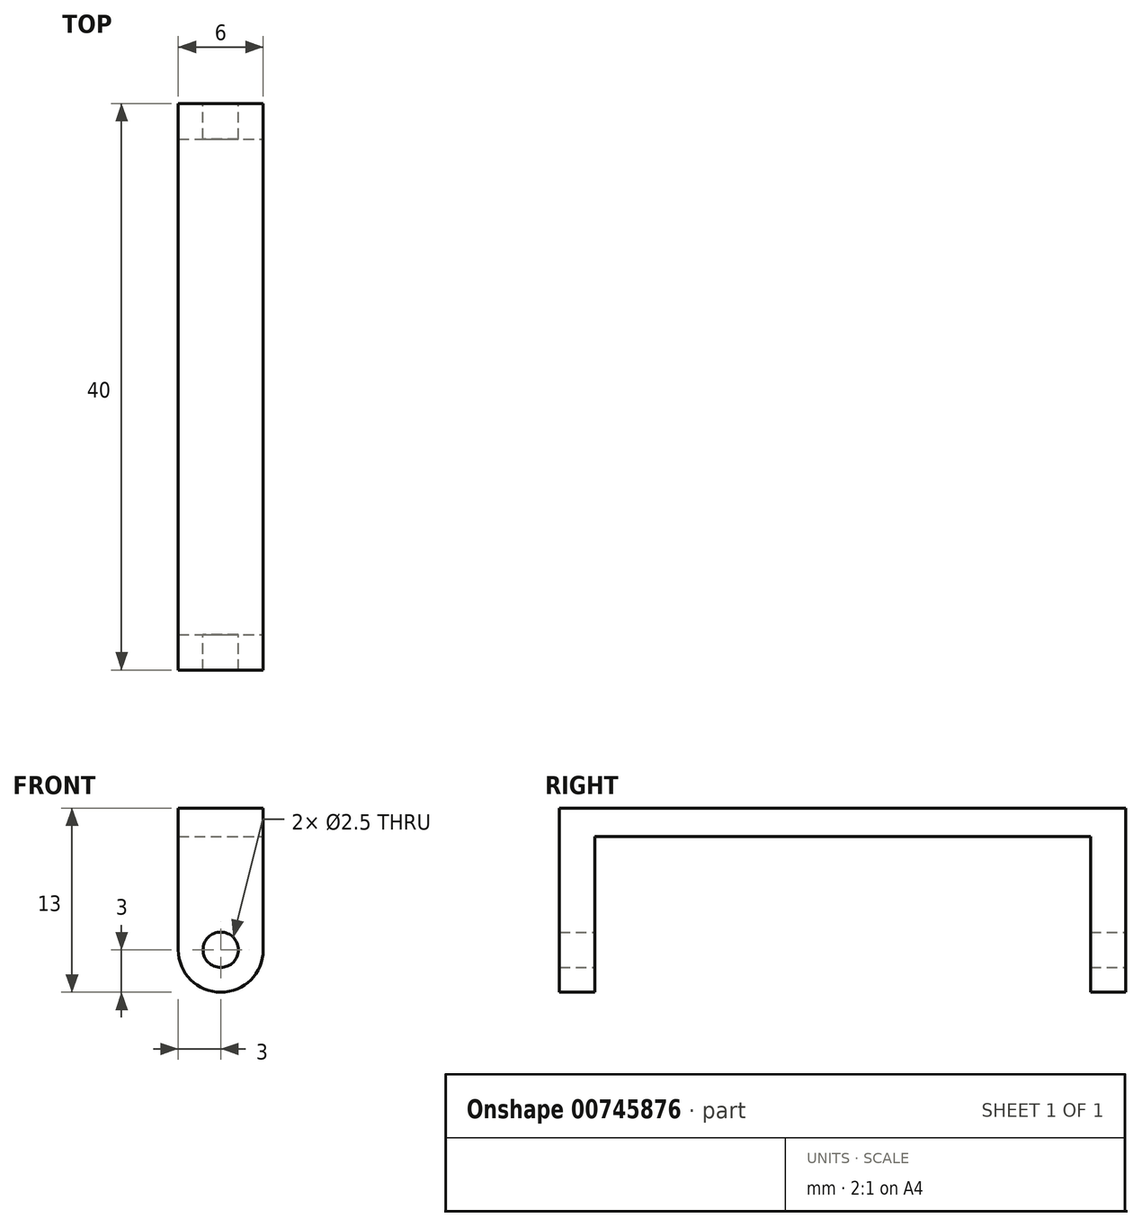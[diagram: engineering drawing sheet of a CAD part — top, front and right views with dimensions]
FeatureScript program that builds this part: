
annotation { "Feature Type Name" : "Feature", "Feature Type Description" : "" }
export const myFeature = defineFeature(function(context is Context, id is Id, definition is map)
    precondition{}
    {
        {
            var Q0;
            Q0=qCreatedBy(makeId("Front.planeOp"),FACE);
            var sketch = newSketch(context, id + "F0", { "sketchPlane" : qUnion([Q0])});
            skCircle(sketch, "E0", {"center": v(0, 0) * mm, "radius": 1.25 * mm});
            skLineSegment(sketch, "E1", {"start": v(-3, 0) * mm, "end": v(-3, 10) * mm});
            skLineSegment(sketch, "E2", {"start": v(-3, 10) * mm, "end": v(3, 10) * mm});
            skLineSegment(sketch, "E3", {"start": v(3, 10) * mm, "end": v(3, 0) * mm});
            skLineSegment(sketch, "E4", {"start": v(-3, 8) * mm, "end": v(3, 8) * mm});
            skArc(sketch, "E5", {"start": v(-3, 0) * mm, "mid": v(0, -3) * mm, "end": v(3, 0) * mm});
            skSolve(sketch);
        }
        {
            var Q0;
            {var subQ0=sQuery(id+"F0.wireOp",EDGE,"E2");Q0=makeQuery(id+"F0.imprint","IMPRINT",FACE,{"disambiguationData":[TD([[makeQuery(id+"F0.imprint","IMPRINT",EDGE,{"derivedFrom":subQ0}),-1.0]])]});}
            extrude(context, id + "F1", {"entities" : qUnion([Q0]), "depth" : 40 * mm, "offsetDistance" : 25 * mm});
        }
        {
            var Q0;
            Q0=makeQuery(id+"F0.imprint","IMPRINT",FACE,{"disambiguationData":[TD([[makeQuery(id+"F0.imprint","IMPRINT",EDGE,{"derivedFrom":sQuery(id+"F0.wireOp",EDGE,"E0")}),-1.0]])]});
            extrude(context, id + "F2", {"entities" : qUnion([Q0]), "operationType" : NewBodyOperationType.ADD, "depth" : 2.5 * mm, "offsetDistance" : 25 * mm});
        }
        {
            var Q0;
            Q0=makeQuery(id+"F0.imprint","IMPRINT",FACE,{"disambiguationData":[TD([[makeQuery(id+"F0.imprint","IMPRINT",EDGE,{"derivedFrom":sQuery(id+"F0.wireOp",EDGE,"E0")}),-1.0]])]});
            extrude(context, id + "F3", {"entities" : qUnion([Q0]), "operationType" : NewBodyOperationType.ADD, "depth" : 40 * mm, "offsetDistance" : 25 * mm, "hasSecondDirection" : true, "secondDirectionOppositeDirection" : false, "secondDirectionDepth" : 37.5 * mm});
        }
    });
